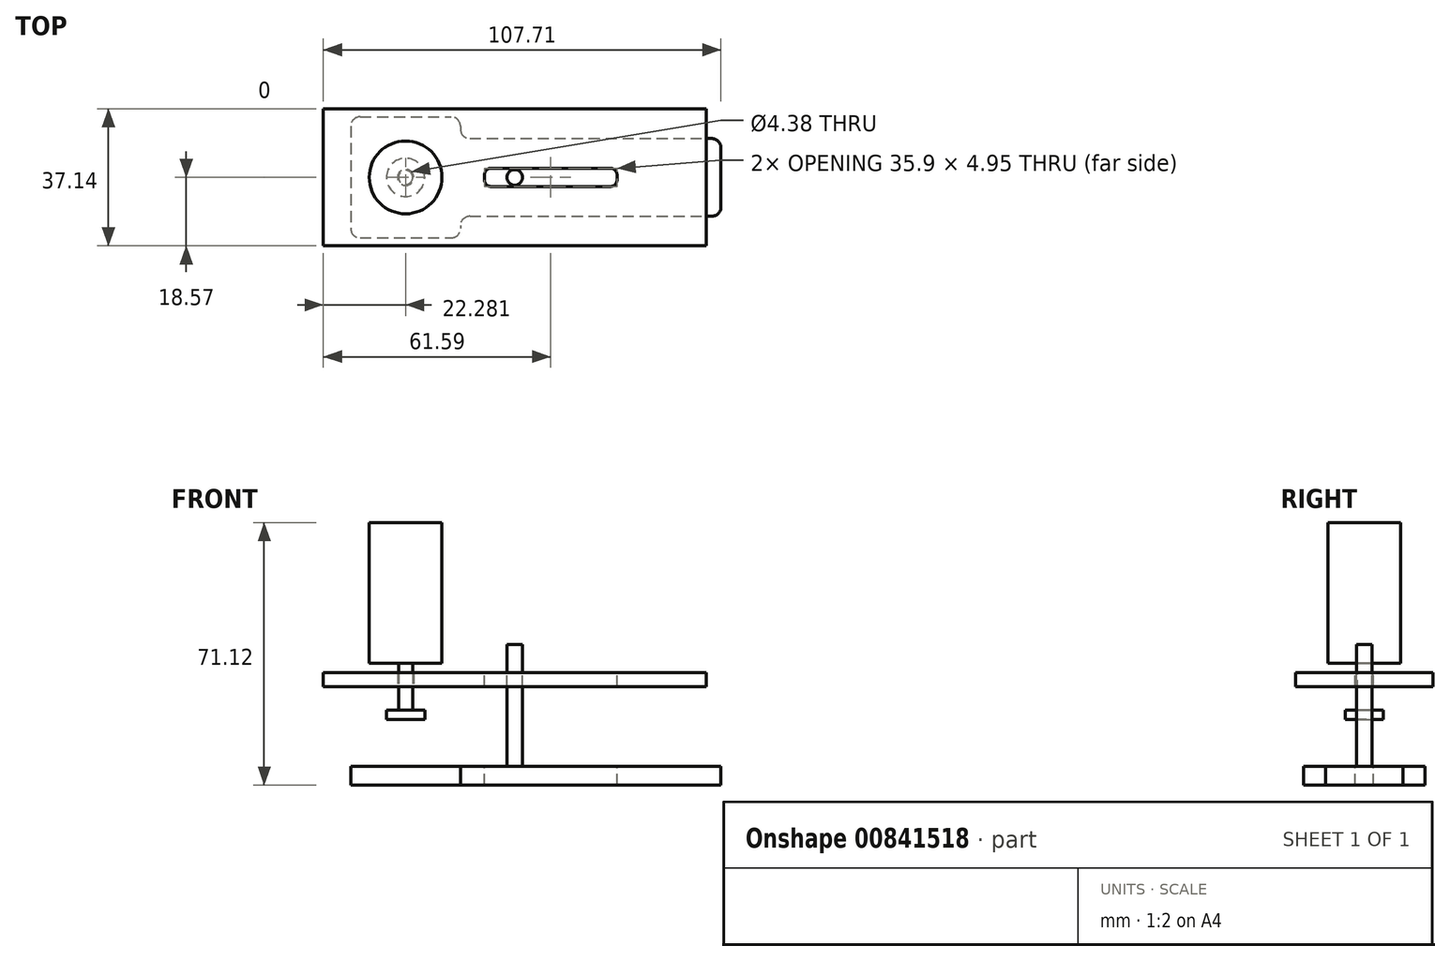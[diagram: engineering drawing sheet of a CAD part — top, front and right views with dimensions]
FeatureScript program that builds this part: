
annotation { "Feature Type Name" : "Feature", "Feature Type Description" : "" }
export const myFeature = defineFeature(function(context is Context, id is Id, definition is map)
    precondition{}
    {
        {
            var Q0;
            Q0=qCreatedBy(makeId("Top.planeOp"),FACE);
            var sketch = newSketch(context, id + "F0", { "sketchPlane" : qUnion([Q0])});
            skLineSegment(sketch, "E0.bottom", {"start": v(-44.42, 16.4) * mm, "end": v(-14.7, 16.4) * mm});
            skLineSegment(sketch, "E0.top", {"start": v(-44.42, -16.4) * mm, "end": v(-14.7, -16.4) * mm});
            skLineSegment(sketch, "E0.left", {"start": v(-44.42, 16.4) * mm, "end": v(-44.42, -16.4) * mm});
            skLineSegment(sketch, "E0.right", {"start": v(-14.7, 16.4) * mm, "end": v(-14.7, -16.4) * mm});
            skPoint(sketch, "E0.middle", {"position": v(-29.56, 0) * mm});
            skLineSegment(sketch, "E1.bottom", {"start": v(-14.7, 10.52) * mm, "end": v(55.87, 10.52) * mm});
            skLineSegment(sketch, "E1.top", {"start": v(-14.7, -10.52) * mm, "end": v(55.87, -10.52) * mm});
            skLineSegment(sketch, "E1.left", {"start": v(-14.7, 10.52) * mm, "end": v(-14.7, -10.52) * mm});
            skLineSegment(sketch, "E1.right", {"start": v(55.87, 10.52) * mm, "end": v(55.87, -10.52) * mm});
            skPoint(sketch, "E1.middle", {"position": v(20.58, 0) * mm});
            skSolve(sketch);
        }
        {
            var Q0;
            Q0 = qSketchRegion(id + "F0", true);
            extrude(context, id + "F1", {"entities" : qUnion([Q0]), "depth" : 5.08 * mm, "offsetDistance" : 25.4 * mm});
        }
        {
            var Q0;
            Q0=makeQuery(id+"F1.opExtrude","SWEPT_EDGE",EDGE,{"disambiguationData":[OSD([sQuery(id+"F0.wireOp",EDGE,"E0.right"),sQuery(id+"F0.wireOp",EDGE,"E1.bottom"),sQuery(id+"F0.wireOp",EDGE,"E1.left")])]});
            var Q1;
            Q1=makeQuery(id+"F1.opExtrude","SWEPT_EDGE",EDGE,{"disambiguationData":[OSD([sQuery(id+"F0.wireOp",EDGE,"E0.bottom"),sQuery(id+"F0.wireOp",EDGE,"E0.right")])]});
            var Q2;
            Q2=makeQuery(id+"F1.opExtrude","SWEPT_EDGE",EDGE,{"disambiguationData":[OSD([sQuery(id+"F0.wireOp",EDGE,"E0.bottom"),sQuery(id+"F0.wireOp",EDGE,"E0.left")])]});
            var Q3;
            Q3=makeQuery(id+"F1.opExtrude","SWEPT_EDGE",EDGE,{"disambiguationData":[OSD([sQuery(id+"F0.wireOp",EDGE,"E1.bottom"),sQuery(id+"F0.wireOp",EDGE,"E1.right")])]});
            var Q4;
            Q4=makeQuery(id+"F1.opExtrude","SWEPT_EDGE",EDGE,{"disambiguationData":[OSD([sQuery(id+"F0.wireOp",EDGE,"E1.top"),sQuery(id+"F0.wireOp",EDGE,"E1.right")])]});
            var Q5;
            Q5=makeQuery(id+"F1.opExtrude","SWEPT_EDGE",EDGE,{"disambiguationData":[OSD([sQuery(id+"F0.wireOp",EDGE,"E0.right"),sQuery(id+"F0.wireOp",EDGE,"E1.top"),sQuery(id+"F0.wireOp",EDGE,"E1.left")])]});
            var Q6;
            Q6=makeQuery(id+"F1.opExtrude","SWEPT_EDGE",EDGE,{"disambiguationData":[OSD([sQuery(id+"F0.wireOp",EDGE,"E0.top"),sQuery(id+"F0.wireOp",EDGE,"E0.right")])]});
            var Q7;
            Q7=makeQuery(id+"F1.opExtrude","SWEPT_EDGE",EDGE,{"disambiguationData":[OSD([sQuery(id+"F0.wireOp",EDGE,"E0.top"),sQuery(id+"F0.wireOp",EDGE,"E0.left")])]});
            fillet(context, id + "F2", {"entities" : qUnion([Q0, Q1, Q2, Q3, Q4, Q5, Q6, Q7]), "radius" : 2.54 * mm, "tangentPropagation" : true, "allowEdgeOverflow" : false});
        }
        {
            var Q0;
            Q0=makeQuery(id+"F1.opExtrude","CAP_FACE",FACE,{"disambiguationData":[OSD([sQuery(id+"F0.wireOp",EDGE,"E0.bottom"),sQuery(id+"F0.wireOp",EDGE,"E0.top"),sQuery(id+"F0.wireOp",EDGE,"E0.left"),sQuery(id+"F0.wireOp",EDGE,"E0.right"),sQuery(id+"F0.wireOp",EDGE,"E1.bottom"),sQuery(id+"F0.wireOp",EDGE,"E1.top"),sQuery(id+"F0.wireOp",EDGE,"E1.right")])],"isStart":false});
            cPlane(context, id + "F3", {"entities" : qUnion([Q0]), "cplaneType" : CPlaneType.OFFSET, "offset" : 12.7 * mm, "width" : 152.4 * mm, "height" : 152.4 * mm});
        }
        {
            var Q0;
            Q0=qCreatedBy(id+"F3.planeOp",FACE);
            var sketch = newSketch(context, id + "F4", { "sketchPlane" : qUnion([Q0])});
            skCircle(sketch, "E2", {"center": v(-29.56, 0) * mm, "radius": 5.19 * mm});
            skSolve(sketch);
        }
        {
            var Q0;
            Q0 = qSketchRegion(id + "F4", true);
            extrude(context, id + "F5", {"entities" : qUnion([Q0]), "depth" : 2.54 * mm, "offsetDistance" : 25.4 * mm});
        }
        {
            var Q0;
            Q0=makeQuery(id+"F5.opExtrude","CAP_FACE",FACE,{"disambiguationData":[OSD([sQuery(id+"F4.wireOp",EDGE,"E2")])],"isStart":false});
            var sketch = newSketch(context, id + "F6", { "sketchPlane" : qUnion([Q0])});
            skCircle(sketch, "E3.0", {"center": v(-29.56, 0) * mm, "radius": 5.19 * mm});
            skCircle(sketch, "E4", {"center": v(-29.56, 0) * mm, "radius": 1.93 * mm});
            skSolve(sketch);
        }
        {
            var Q0;
            Q0=makeQuery(id+"F6.imprint","IMPRINT",FACE,{"disambiguationData":[TD([[makeQuery(id+"F6.imprint","IMPRINT",EDGE,{"derivedFrom":sQuery(id+"F6.wireOp",EDGE,"E4")}),1.0]])]});
            extrude(context, id + "F7", {"entities" : qUnion([Q0]), "depth" : 12.7 * mm, "offsetDistance" : 25.4 * mm});
        }
        {
            var Q0;
            Q0=makeQuery(id+"F7.opExtrude","CAP_FACE",FACE,{"disambiguationData":[OSD([sQuery(id+"F6.wireOp",EDGE,"E4")])],"isStart":false});
            var sketch = newSketch(context, id + "F8", { "sketchPlane" : qUnion([Q0])});
            skCircle(sketch, "E5.0", {"center": v(-29.56, 0) * mm, "radius": 1.93 * mm});
            skCircle(sketch, "E6", {"center": v(-29.56, 0) * mm, "radius": 9.87 * mm});
            skSolve(sketch);
        }
        {
            var Q0;
            Q0 = qSketchRegion(id + "F8", true);
            var Q1;
            Q1=makeQuery(id+"F8.imprint","IMPRINT",FACE,{"disambiguationData":[TD([[makeQuery(id+"F8.imprint","IMPRINT",EDGE,{"derivedFrom":sQuery(id+"F8.wireOp",EDGE,"E5.0")}),1.0]])]});
            extrude(context, id + "F9", {"entities" : qUnion([Q0, Q1]), "operationType" : NewBodyOperationType.ADD, "depth" : 38.1 * mm, "offsetDistance" : 25.4 * mm});
        }
        {
            var Q0;
            Q0=makeQuery(id+"F9.opExtrude","CAP_FACE",FACE,{"disambiguationData":[OSD([sQuery(id+"F8.wireOp",EDGE,"E6")])],"isStart":true});
            cPlane(context, id + "F10", {"entities" : qUnion([Q0]), "cplaneType" : CPlaneType.OFFSET, "offset" : 2.54 * mm, "width" : 152.4 * mm, "height" : 152.4 * mm});
        }
        {
            var Q0;
            Q0=qCreatedBy(id+"F10.planeOp",FACE);
            var sketch = newSketch(context, id + "F11", { "sketchPlane" : qUnion([Q0])});
            skLineSegment(sketch, "E7.bottom", {"start": v(-51.84, 18.57) * mm, "end": v(51.84, 18.57) * mm});
            skLineSegment(sketch, "E7.top", {"start": v(-51.84, -18.57) * mm, "end": v(51.84, -18.57) * mm});
            skLineSegment(sketch, "E7.left", {"start": v(-51.84, 18.57) * mm, "end": v(-51.84, -18.57) * mm});
            skLineSegment(sketch, "E7.right", {"start": v(51.84, 18.57) * mm, "end": v(51.84, -18.57) * mm});
            skPoint(sketch, "E7.middle", {"position": v(0, 0) * mm});
            skSolve(sketch);
        }
        {
            var Q0;
            Q0 = qSketchRegion(id + "F11", true);
            extrude(context, id + "F12", {"entities" : qUnion([Q0]), "depth" : 3.8 * mm, "offsetDistance" : 25.4 * mm});
        }
        {
            var Q0;
            Q0=makeQuery(id+"F7.opExtrude","SWEPT_BODY",BODY,{"disambiguationData":[OSD([sQuery(id+"F6.wireOp",EDGE,"E4")])]});
            var Q1;
            Q1=makeQuery(id+"F12.opExtrude","SWEPT_BODY",BODY,{"disambiguationData":[OSD([sQuery(id+"F11.wireOp",EDGE,"E7.bottom"),sQuery(id+"F11.wireOp",EDGE,"E7.top"),sQuery(id+"F11.wireOp",EDGE,"E7.left"),sQuery(id+"F11.wireOp",EDGE,"E7.right")])]});
            booleanBodies(context, id + "F13", {"operationType" : BooleanOperationType.SUBTRACTION, "tools" : qUnion([Q0]), "targets" : qUnion([Q1]), "offset" : true, "offsetAll" : true, "offsetDistance" : 0.25 * mm, "keepTools" : true});
        }
        {
            var Q0;
            Q0=makeQuery(id+"F12.opExtrude","CAP_FACE",FACE,{"disambiguationData":[OSD([sQuery(id+"F11.wireOp",EDGE,"E7.bottom"),sQuery(id+"F11.wireOp",EDGE,"E7.top"),sQuery(id+"F11.wireOp",EDGE,"E7.left"),sQuery(id+"F11.wireOp",EDGE,"E7.right")])],"isStart":true});
            var sketch = newSketch(context, id + "F14", { "sketchPlane" : qUnion([Q0])});
            skLineSegment(sketch, "E8.bottom", {"start": v(-8.2, 2.48) * mm, "end": v(27.7, 2.48) * mm});
            skLineSegment(sketch, "E8.top", {"start": v(-8.2, -2.48) * mm, "end": v(27.7, -2.48) * mm});
            skLineSegment(sketch, "E8.left", {"start": v(-8.2, 2.48) * mm, "end": v(-8.2, -2.48) * mm});
            skLineSegment(sketch, "E8.right", {"start": v(27.7, 2.48) * mm, "end": v(27.7, -2.48) * mm});
            skPoint(sketch, "E8.middle", {"position": v(9.75, 0) * mm});
            skSolve(sketch);
        }
        {
            var Q0;
            Q0 = qSketchRegion(id + "F14", true);
            extrude(context, id + "F15", {"entities" : qUnion([Q0]), "operationType" : NewBodyOperationType.REMOVE, "endBound" : BoundingType.THROUGH_ALL, "oppositeDirection" : true, "depth" : 25.4 * mm, "offsetDistance" : 25.4 * mm});
        }
        {
            var Q0;
            Q0=makeQuery(id+"F15.boolean.opBoolean","COPY",EDGE,{"derivedFrom":makeQuery(id+"F15.opExtrude","SWEPT_EDGE",EDGE,{"disambiguationData":[OSD([sQuery(id+"F14.wireOp",EDGE,"E8.bottom"),sQuery(id+"F14.wireOp",EDGE,"E8.left")])]})});
            var Q1;
            Q1=makeQuery(id+"F15.boolean.opBoolean","COPY",EDGE,{"derivedFrom":makeQuery(id+"F15.opExtrude","SWEPT_EDGE",EDGE,{"disambiguationData":[OSD([sQuery(id+"F14.wireOp",EDGE,"E8.top"),sQuery(id+"F14.wireOp",EDGE,"E8.left")])]})});
            var Q2;
            Q2=makeQuery(id+"F15.boolean.opBoolean","COPY",EDGE,{"derivedFrom":makeQuery(id+"F15.opExtrude","SWEPT_EDGE",EDGE,{"disambiguationData":[OSD([sQuery(id+"F14.wireOp",EDGE,"E8.bottom"),sQuery(id+"F14.wireOp",EDGE,"E8.right")])]})});
            var Q3;
            Q3=makeQuery(id+"F15.boolean.opBoolean","COPY",EDGE,{"derivedFrom":makeQuery(id+"F15.opExtrude","SWEPT_EDGE",EDGE,{"disambiguationData":[OSD([sQuery(id+"F14.wireOp",EDGE,"E8.top"),sQuery(id+"F14.wireOp",EDGE,"E8.right")])]})});
            fillet(context, id + "F16", {"entities" : qUnion([Q0, Q1, Q2, Q3]), "radius" : 1.78 * mm, "tangentPropagation" : true, "allowEdgeOverflow" : false});
        }
        {
            var Q0;
            Q0=makeQuery(id+"F12.opExtrude","CAP_FACE",FACE,{"disambiguationData":[OSD([sQuery(id+"F11.wireOp",EDGE,"E7.bottom"),sQuery(id+"F11.wireOp",EDGE,"E7.top"),sQuery(id+"F11.wireOp",EDGE,"E7.left"),sQuery(id+"F11.wireOp",EDGE,"E7.right")])],"isStart":true});
            var sketch = newSketch(context, id + "F17", { "sketchPlane" : qUnion([Q0])});
            skCircle(sketch, "E9", {"center": v(0, 0) * mm, "radius": 2.12 * mm});
            skSolve(sketch);
        }
        {
            var Q0;
            Q0 = qSketchRegion(id + "F17", true);
            var Q1;
            Q1=makeQuery(id+"F1.opExtrude","CAP_FACE",FACE,{"disambiguationData":[OSD([sQuery(id+"F0.wireOp",EDGE,"E0.bottom"),sQuery(id+"F0.wireOp",EDGE,"E0.top"),sQuery(id+"F0.wireOp",EDGE,"E0.left"),sQuery(id+"F0.wireOp",EDGE,"E0.right"),sQuery(id+"F0.wireOp",EDGE,"E1.bottom"),sQuery(id+"F0.wireOp",EDGE,"E1.top"),sQuery(id+"F0.wireOp",EDGE,"E1.right")])],"isStart":false});
            extrude(context, id + "F18", {"entities" : qUnion([Q0]), "operationType" : NewBodyOperationType.ADD, "endBound" : BoundingType.UP_TO_SURFACE, "oppositeDirection" : true, "depth" : 25.4 * mm, "endBoundEntityFace" : qUnion([Q1]), "offsetDistance" : 25.4 * mm});
        }
        {
            var Q0;
            Q0=makeQuery(id+"F18.opExtrude","CAP_FACE",FACE,{"disambiguationData":[OSD([sQuery(id+"F17.wireOp",EDGE,"E9")])],"isStart":true});
            extrude(context, id + "F19", {"entities" : qUnion([Q0]), "operationType" : NewBodyOperationType.ADD, "depth" : 7.62 * mm, "offsetDistance" : 25.4 * mm});
        }
    });
